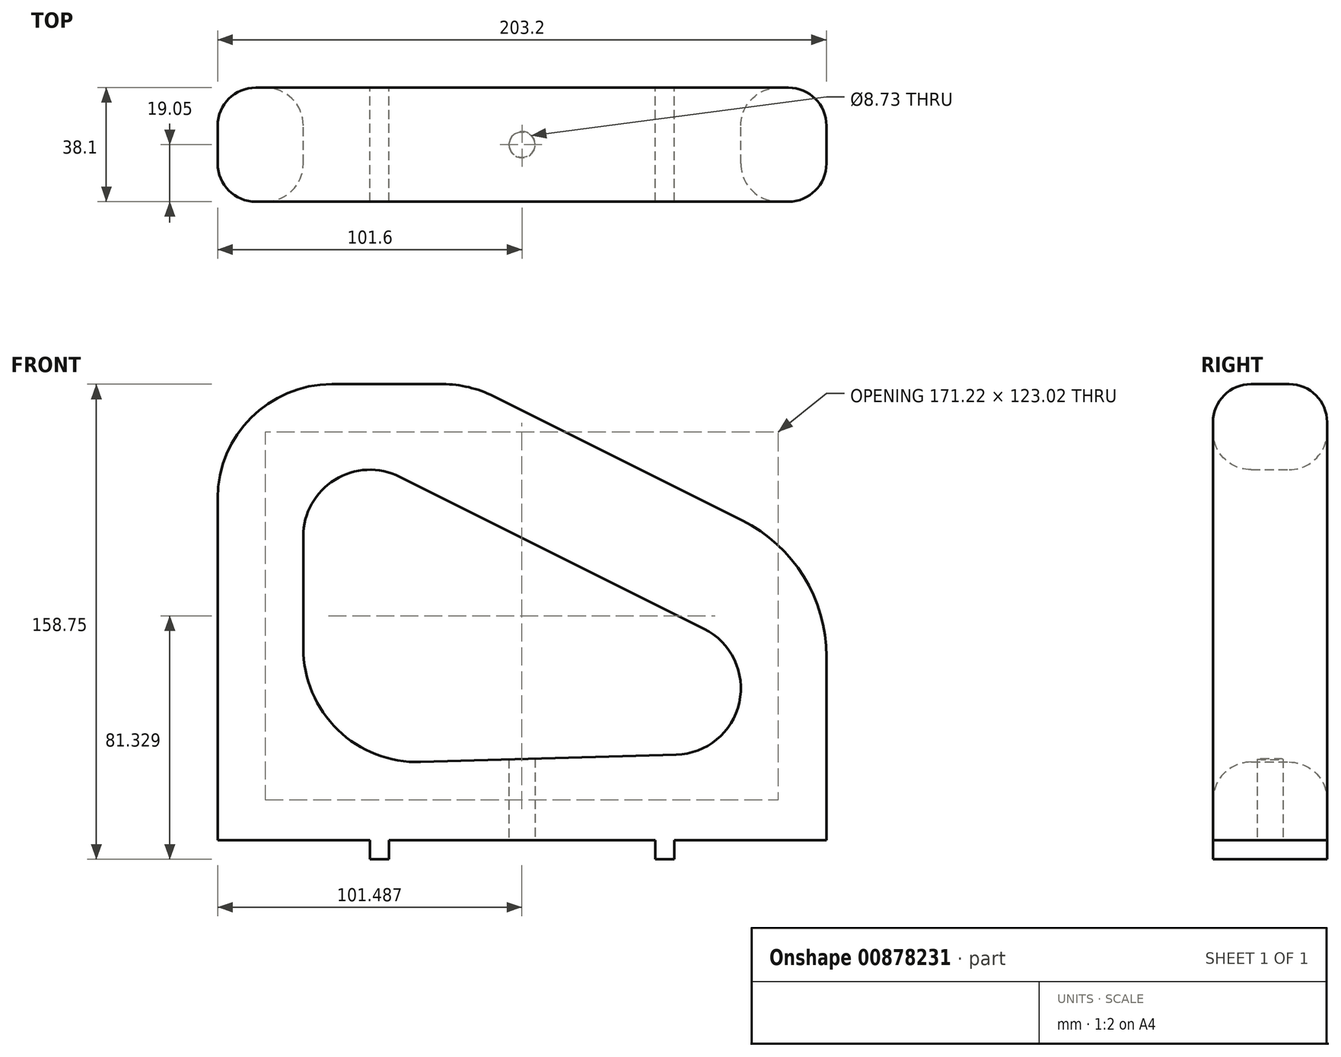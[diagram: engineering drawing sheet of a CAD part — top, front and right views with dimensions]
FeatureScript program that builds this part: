
annotation { "Feature Type Name" : "Feature", "Feature Type Description" : "" }
export const myFeature = defineFeature(function(context is Context, id is Id, definition is map)
    precondition{}
    {
        {
            var Q0;
            Q0=qCreatedBy(makeId("Front.planeOp"),FACE);
            var sketch = newSketch(context, id + "F0", { "sketchPlane" : qUnion([Q0])});
            skLineSegment(sketch, "E0.bottom", {"start": v(0, 0) * mm, "end": v(203.2, 0) * mm});
            skLineSegment(sketch, "E0.top", {"start": v(38.1, 152.4) * mm, "end": v(75.1, 152.4) * mm});
            skLineSegment(sketch, "E0.left", {"start": v(0, 0) * mm, "end": v(0, 114.3) * mm});
            skLineSegment(sketch, "E0.right", {"start": v(203.2, 0) * mm, "end": v(203.2, 61.45) * mm});
            skArc(sketch, "E1", {"start": v(60.74, 121.48) * mm, "mid": v(39.12, 120.5) * mm, "end": v(28.57, 101.6) * mm});
            skArc(sketch, "E2", {"start": v(153.03, 28.58) * mm, "mid": v(174.1, 46) * mm, "end": v(162.34, 70.68) * mm});
            skLineSegment(sketch, "E3", {"start": v(60.74, 121.48) * mm, "end": v(162.34, 70.68) * mm});
            skLineSegment(sketch, "E4", {"start": v(92.14, 148.38) * mm, "end": v(175.12, 106.89) * mm});
            skPoint(sketch, "E5.visualSharp", {"position": v(84.1, 152.4) * mm});
            skArc(sketch, "E5.filletArc", {"start": v(92.14, 148.38) * mm, "mid": v(83.85, 151.38) * mm, "end": v(75.1, 152.4) * mm});
            skPoint(sketch, "E6.visualSharp", {"position": v(203.2, 92.85) * mm});
            skArc(sketch, "E6.filletArc", {"start": v(203.2, 61.45) * mm, "mid": v(195.61, 88.16) * mm, "end": v(175.12, 106.89) * mm});
            skPoint(sketch, "E7.visualSharp", {"position": v(0, 152.4) * mm});
            skArc(sketch, "E7.filletArc", {"start": v(38.1, 152.4) * mm, "mid": v(11.16, 141.24) * mm, "end": v(0, 114.3) * mm});
            skLineSegment(sketch, "E8", {"start": v(28.57, 101.6) * mm, "end": v(28.57, 64.25) * mm});
            skLineSegment(sketch, "E9", {"start": v(153.03, 28.58) * mm, "end": v(67.76, 26.16) * mm});
            skPoint(sketch, "E10.visualSharp", {"position": v(28.57, 25.05) * mm});
            skArc(sketch, "E10.filletArc", {"start": v(28.57, 64.25) * mm, "mid": v(40.12, 36.93) * mm, "end": v(67.76, 26.16) * mm});
            skSolve(sketch);
        }
        {
            var Q0;
            Q0 = qSketchRegion(id + "F0", true);
            extrude(context, id + "F1", {"entities" : qUnion([Q0]), "depth" : 38.1 * mm, "offsetDistance" : 25.4 * mm});
        }
        {
            var Q0;
            Q0=makeQuery(id+"F1.opExtrude","CAP_EDGE",EDGE,{"disambiguationData":[OSD([sQuery(id+"F0.wireOp",EDGE,"E0.top")])],"isStart":false});
            var Q1;
            Q1=makeQuery(id+"F1.opExtrude","CAP_EDGE",EDGE,{"disambiguationData":[OSD([sQuery(id+"F0.wireOp",EDGE,"E3")])],"isStart":false});
            var Q2;
            Q2=makeQuery(id+"F1.opExtrude","CAP_EDGE",EDGE,{"disambiguationData":[OSD([sQuery(id+"F0.wireOp",EDGE,"E3")])],"isStart":true});
            var Q3;
            Q3=makeQuery(id+"F1.opExtrude","CAP_EDGE",EDGE,{"disambiguationData":[OSD([sQuery(id+"F0.wireOp",EDGE,"E4")])],"isStart":true});
            fillet(context, id + "F2", {"entities" : qUnion([Q0, Q1, Q2, Q3]), "radius" : 12.7 * mm, "tangentPropagation" : true, "allowEdgeOverflow" : false});
        }
        {
            var Q0;
            Q0=makeQuery(id+"F1.opExtrude","SWEPT_FACE",FACE,{"disambiguationData":[OSD([sQuery(id+"F0.wireOp",EDGE,"E0.bottom")])]});
            var sketch = newSketch(context, id + "F3", { "sketchPlane" : qUnion([Q0])});
            skCircle(sketch, "E11", {"center": v(101.6, 19.05) * mm, "radius": 4.37 * mm});
            skLineSegment(sketch, "E12", {"start": v(101.6, 38.1) * mm, "end": v(101.6, 0) * mm, "construction": true});
            skLineSegment(sketch, "E13", {"start": v(101.6, 19.05) * mm, "end": v(203.2, 19.05) * mm, "construction": true});
            skSolve(sketch);
        }
        {
            var Q0;
            Q0 = qSketchRegion(id + "F3", true);
            extrude(context, id + "F4", {"entities" : qUnion([Q0]), "operationType" : NewBodyOperationType.REMOVE, "endBound" : BoundingType.UP_TO_NEXT, "oppositeDirection" : true, "depth" : 25.4 * mm, "offsetDistance" : 25.4 * mm});
        }
        {
            var Q0;
            Q0=makeQuery(id+"F1.opExtrude","SWEPT_FACE",FACE,{"disambiguationData":[OSD([sQuery(id+"F0.wireOp",EDGE,"E0.bottom")])]});
            var sketch = newSketch(context, id + "F5", { "sketchPlane" : qUnion([Q0])});
            skLineSegment(sketch, "E14.bottom", {"start": v(50.8, 38.1) * mm, "end": v(57.15, 38.1) * mm});
            skLineSegment(sketch, "E14.top", {"start": v(50.8, 0) * mm, "end": v(57.15, 0) * mm});
            skLineSegment(sketch, "E14.left", {"start": v(50.8, 38.1) * mm, "end": v(50.8, 0) * mm});
            skLineSegment(sketch, "E14.right", {"start": v(57.15, 38.1) * mm, "end": v(57.15, 0) * mm});
            skLineSegment(sketch, "E15", {"start": v(101.6, 38.1) * mm, "end": v(101.6, 0) * mm, "construction": true});
            skLineSegment(sketch, "E16.MirrorCS", {"start": v(146.05, 38.1) * mm, "end": v(146.05, 0) * mm});
            skLineSegment(sketch, "E17.MirrorCS", {"start": v(152.4, 38.1) * mm, "end": v(146.05, 38.1) * mm});
            skLineSegment(sketch, "E18.MirrorCS", {"start": v(152.4, 38.1) * mm, "end": v(152.4, 0) * mm});
            skLineSegment(sketch, "E19.MirrorCS", {"start": v(152.4, 0) * mm, "end": v(146.05, 0) * mm});
            skSolve(sketch);
        }
        {
            var Q0;
            Q0 = qSketchRegion(id + "F5", true);
            extrude(context, id + "F6", {"entities" : qUnion([Q0]), "operationType" : NewBodyOperationType.ADD, "depth" : 6.35 * mm, "offsetDistance" : 25.4 * mm});
        }
    });
